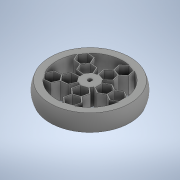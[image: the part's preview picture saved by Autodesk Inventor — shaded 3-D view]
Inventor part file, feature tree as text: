
AUTODESK INVENTOR PART (.ipt)
format: ipt  version: 2020 (Build 240168000, 168)  size: 390,144 bytes
history: native  units: in
note: dims shown in document units (in); Inventor stores cm internally (conversion verified against a paired STEP export)
features: sketch x2, extrude x1, revolve x1, projected_geometry x1
ambient origin geometry x8: Origin, YZ Plane, XZ Plane, XY Plane, X Axis, Y Axis, Z Axis, Center Point
bodies: Solid1 (feature_tree)
feature tree (5):
  extrude  "Extrusion1"  Depth=0.0394in
  revolve  "Revolution1"  [1 undecoded]
  sketch  "Sketch1"  dims[d0=0.1181in d1=0.0394in]
  sketch  "Sketch2"  dims[d2=2.3622in d3=0.1969in d4=0.1969in d11=0.5in d12=0.0in d25=0.0315in d26=0.0315in d27=0.0157in d28=0.0157in d34=90.0deg d35=1.9685in d37=360.0deg d39=0.0591in]
  projected_geometry  "Projected Loop1"
note: 1 required parameter value undecoded (feature->parameter linkage not recoverable at this tier; creation-order binding heuristic only, values carry confidence <= 0.55)
